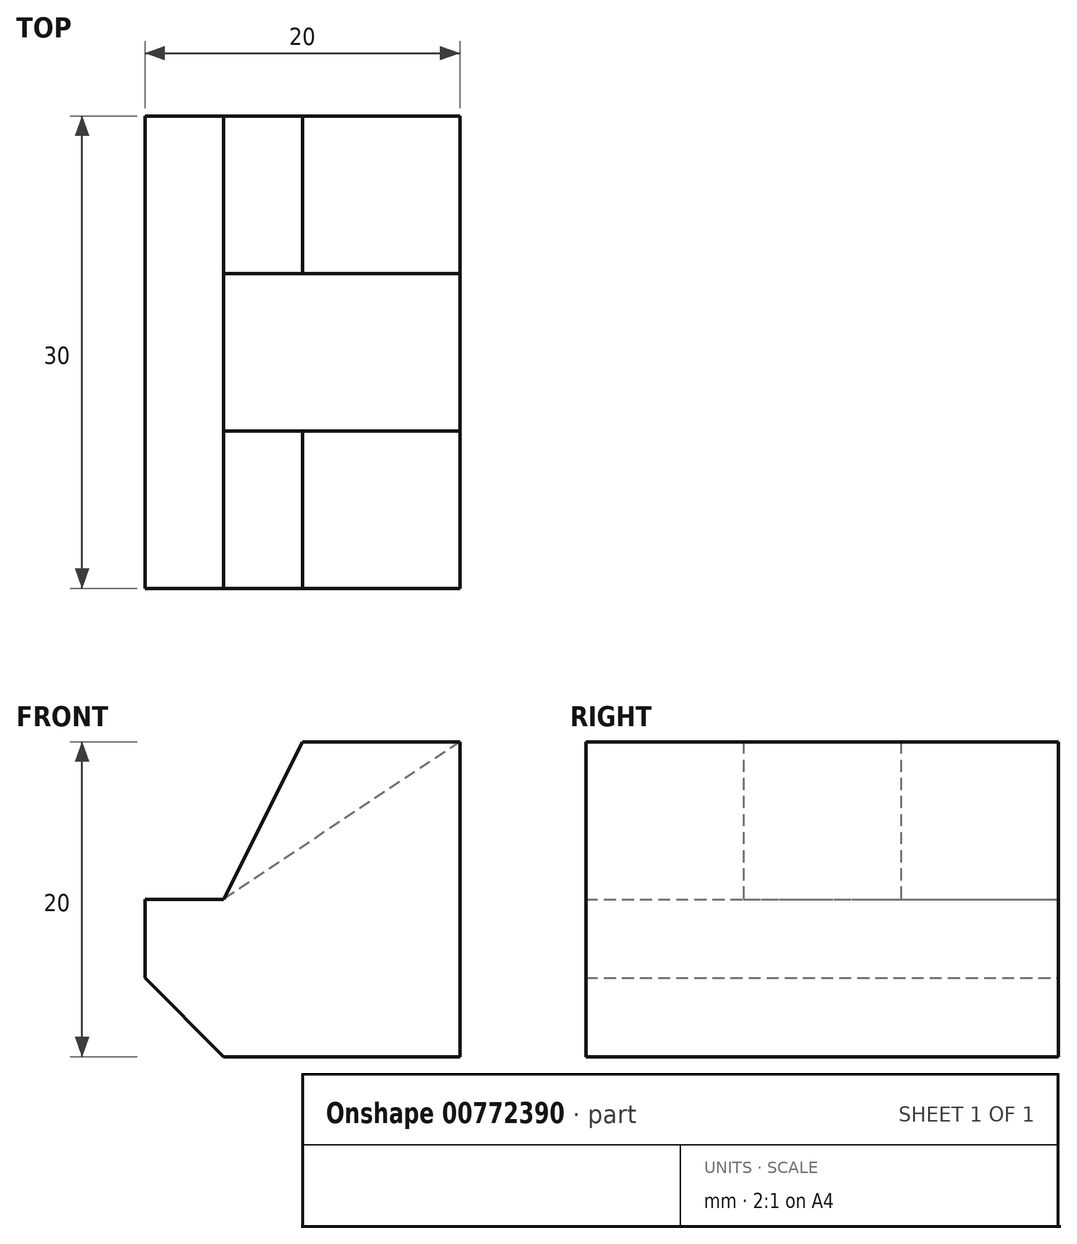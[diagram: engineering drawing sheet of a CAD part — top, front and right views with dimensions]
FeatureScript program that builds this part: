
annotation { "Feature Type Name" : "Feature", "Feature Type Description" : "" }
export const myFeature = defineFeature(function(context is Context, id is Id, definition is map)
    precondition{}
    {
        {
            var Q0;
            Q0=qCreatedBy(makeId("Front.planeOp"),FACE);
            var sketch = newSketch(context, id + "F0", { "sketchPlane" : qUnion([Q0])});
            skLineSegment(sketch, "E0", {"start": v(0, 0) * mm, "end": v(0, 20) * mm});
            skLineSegment(sketch, "E1", {"start": v(0, 20) * mm, "end": v(-10, 20) * mm});
            skLineSegment(sketch, "E2", {"start": v(-10, 20) * mm, "end": v(-15, 10) * mm});
            skLineSegment(sketch, "E3", {"start": v(-15, 10) * mm, "end": v(-20, 10) * mm});
            skLineSegment(sketch, "E4", {"start": v(-20, 10) * mm, "end": v(-20, 5) * mm});
            skLineSegment(sketch, "E5", {"start": v(-20, 5) * mm, "end": v(-15, 0) * mm});
            skLineSegment(sketch, "E6", {"start": v(-15, 0) * mm, "end": v(0, 0) * mm});
            skLineSegment(sketch, "E7", {"start": v(0, 20) * mm, "end": v(-15, 10) * mm});
            skSolve(sketch);
        }
        {
            var Q0;
            Q0=qSketchRegion(id+"F0",true);
            extrude(context, id + "F1", {"entities" : qUnion([Q0]), "endBound" : BoundingType.SYMMETRIC, "depth" : 30 * mm, "offsetDistance" : 25 * mm});
        }
        {
            var Q0;
            Q0=makeQuery(id+"F0.imprint","IMPRINT",FACE,{"disambiguationData":[TD([[makeQuery(id+"F0.imprint","IMPRINT",EDGE,{"derivedFrom":sQuery(id+"F0.wireOp",EDGE,"E1")}),1.0]])]});
            extrude(context, id + "F2", {"entities" : qUnion([Q0]), "operationType" : NewBodyOperationType.REMOVE, "endBound" : BoundingType.SYMMETRIC, "depth" : 10 * mm, "offsetDistance" : 25 * mm});
        }
    });
